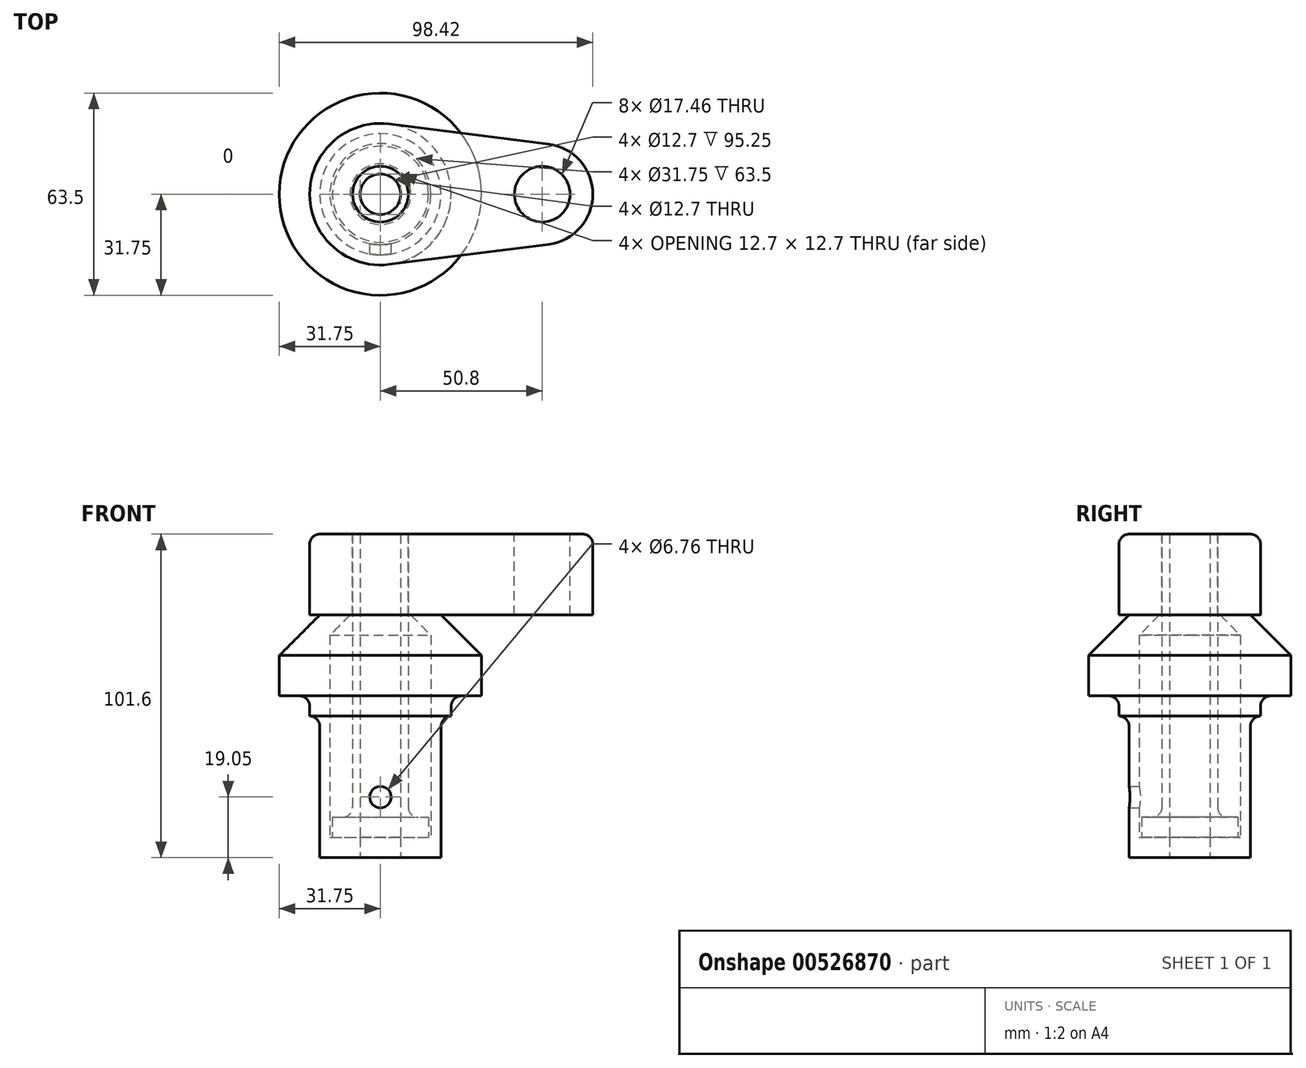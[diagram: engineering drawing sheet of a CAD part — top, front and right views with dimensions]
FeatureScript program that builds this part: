
annotation { "Feature Type Name" : "Feature", "Feature Type Description" : "" }
export const myFeature = defineFeature(function(context is Context, id is Id, definition is map)
    precondition{}
    {
        {
            var Q0;
            Q0=qCreatedBy(makeId("Front.planeOp"),FACE);
            var sketch = newSketch(context, id + "F0", { "sketchPlane" : qUnion([Q0])});
            skLineSegment(sketch, "E0", {"start": v(0, 0) * mm, "end": v(0, 76.2) * mm});
            skLineSegment(sketch, "E1", {"start": v(0, 76.2) * mm, "end": v(19.05, 76.2) * mm});
            skLineSegment(sketch, "E2", {"start": v(19.05, 76.2) * mm, "end": v(31.75, 63.5) * mm});
            skLineSegment(sketch, "E3", {"start": v(31.75, 63.5) * mm, "end": v(31.75, 50.8) * mm});
            skLineSegment(sketch, "E4", {"start": v(31.75, 50.8) * mm, "end": v(22.23, 50.8) * mm});
            skLineSegment(sketch, "E5", {"start": v(22.23, 50.8) * mm, "end": v(22.23, 44.45) * mm});
            skLineSegment(sketch, "E6", {"start": v(22.23, 44.45) * mm, "end": v(19.05, 44.45) * mm});
            skLineSegment(sketch, "E7", {"start": v(19.05, 44.45) * mm, "end": v(19.05, 0) * mm});
            skLineSegment(sketch, "E8", {"start": v(19.05, 0) * mm, "end": v(0, 0) * mm});
            skLineSegment(sketch, "E9", {"start": v(9.53, 76.2) * mm, "end": v(15.88, 69.85) * mm});
            skLineSegment(sketch, "E10", {"start": v(15.88, 69.85) * mm, "end": v(15.88, 6.35) * mm});
            skLineSegment(sketch, "E11", {"start": v(15.88, 6.35) * mm, "end": v(0, 6.35) * mm});
            skLineSegment(sketch, "E12", {"start": v(0, 76.2) * mm, "end": v(0, 92.63) * mm, "construction": true});
            skLineSegment(sketch, "E13", {"start": v(0, 76.2) * mm, "end": v(0, 101.6) * mm});
            skLineSegment(sketch, "E14", {"start": v(0, 101.6) * mm, "end": v(8.73, 101.6) * mm});
            skLineSegment(sketch, "E15", {"start": v(8.73, 101.6) * mm, "end": v(8.73, 12.7) * mm});
            skLineSegment(sketch, "E16", {"start": v(8.73, 12.7) * mm, "end": v(15.08, 12.7) * mm});
            skLineSegment(sketch, "E17", {"start": v(15.08, 12.7) * mm, "end": v(15.08, 6.35) * mm});
            skSolve(sketch);
        }
        {
            var Q0;
            {var subQ4=sQuery(id+"F0.wireOp",EDGE,"E2");Q0=makeQuery(id+"F0.imprint","IMPRINT",FACE,{"disambiguationData":[TD([[makeQuery(id+"F0.imprint","IMPRINT",EDGE,{"derivedFrom":subQ4}),-1.0]])]});}
            var Q1;
            Q1=sQuery(id+"F0.wireOp",EDGE,"E0");
            revolve(context, id + "F1", {"entities" : qUnion([Q0]), "axis" : qUnion([Q1]), "revolveType" : RevolveType.FULL});
        }
        {
            var Q0;
            {var subQ0=sQuery(id+"F0.wireOp",EDGE,"E13");Q0=makeQuery(id+"F0.imprint","IMPRINT",FACE,{"disambiguationData":[TD([[makeQuery(id+"F0.imprint","IMPRINT",EDGE,{"derivedFrom":subQ0}),-1.0]])]});}
            var Q1;
            {var subQ0=sQuery(id+"F0.wireOp",EDGE,"E16");Q1=makeQuery(id+"F0.imprint","IMPRINT",FACE,{"disambiguationData":[TD([[makeQuery(id+"F0.imprint","IMPRINT",EDGE,{"derivedFrom":subQ0}),-1.0]])]});}
            var Q2;
            Q2=sQuery(id+"F0.wireOp",EDGE,"E13");
            revolve(context, id + "F2", {"entities" : qUnion([Q0, Q1]), "axis" : qUnion([Q2]), "revolveType" : RevolveType.FULL});
        }
        {
            var Q0;
            Q0=makeQuery(id+"F2.opRevolve","SWEPT_FACE",FACE,{"disambiguationData":[OSD([sQuery(id+"F0.wireOp",EDGE,"E14")])]});
            var sketch = newSketch(context, id + "F3", { "sketchPlane" : qUnion([Q0])});
            skCircle(sketch, "E18", {"center": v(0, 0) * mm, "radius": 22.23 * mm});
            skCircle(sketch, "E19", {"center": v(50.8, 0) * mm, "radius": 15.88 * mm});
            skLineSegment(sketch, "E20", {"start": v(52.78, -15.75) * mm, "end": v(2.78, -22.05) * mm});
            skLineSegment(sketch, "E21", {"start": v(2.78, 22.05) * mm, "end": v(52.78, 15.75) * mm});
            skCircle(sketch, "E22.0", {"center": v(0, 0) * mm, "radius": 8.73 * mm});
            skCircle(sketch, "E23", {"center": v(50.8, 0) * mm, "radius": 8.73 * mm});
            skSolve(sketch);
        }
        {
            var Q0;
            Q0 = qSketchRegion(id + "F3", true);
            var Q1;
            Q1=makeQuery(id+"F1.opRevolve","SWEPT_FACE",FACE,{"disambiguationData":[OSD([sQuery(id+"F0.wireOp",EDGE,"E1")])]});
            extrude(context, id + "F4", {"entities" : qUnion([Q0]), "oppositeDirection" : true, "depth" : 25.4 * mm, "endBoundEntityFace" : qUnion([Q1]), "offsetDistance" : 0.8 * mm});
        }
        {
            var Q0;
            Q0=qCreatedBy(makeId("Front.planeOp"),FACE);
            var sketch = newSketch(context, id + "F5", { "sketchPlane" : qUnion([Q0])});
            skPoint(sketch, "E24", {"position": v(0, 19.05) * mm});
            skSolve(sketch);
        }
        {
            var Q0;
            Q0=sQuery(id+"F5.wireOp",VERTEX,"E24");
            var Q1;
            Q1=makeQuery(id+"F1.opRevolve","SWEPT_BODY",BODY,{"disambiguationData":[OSD([sQuery(id+"F0.wireOp",EDGE,"E0"),sQuery(id+"F0.wireOp",EDGE,"E1"),sQuery(id+"F0.wireOp",EDGE,"E2"),sQuery(id+"F0.wireOp",EDGE,"E3"),sQuery(id+"F0.wireOp",EDGE,"E4"),sQuery(id+"F0.wireOp",EDGE,"E5"),sQuery(id+"F0.wireOp",EDGE,"E6"),sQuery(id+"F0.wireOp",EDGE,"E7"),sQuery(id+"F0.wireOp",EDGE,"E8"),sQuery(id+"F0.wireOp",EDGE,"E9"),sQuery(id+"F0.wireOp",EDGE,"E10"),sQuery(id+"F0.wireOp",EDGE,"E11")])]});
            hole(context, id + "F6", {"style" : HoleStyle.SIMPLE, "endStyle" : HoleEndStyle.THROUGH, "oppositeDirection" : true, "standardTappedOrClearance" : lookupTablePath({ "standard" : "ANSI", "fit" : "Normal (ASME)", "size" : "1/4", "type" : "Clearance" }), "standardBlindInLast" : lookupTablePath({ "fit" : "Free", "standard" : "ANSI", "size" : "1/4", "type" : "Clearance" }), "holeDiameter" : 6.76 * mm, "tappedDepth" : 14.3 * mm, "tapClearance" : 3, "locations" : qUnion([Q0]), "scope" : qUnion([Q1])});
        }
        {
            var Q0;
            Q0=makeQuery(id+"F4.opExtrude","CAP_EDGE",EDGE,{"disambiguationData":[OSD([sQuery(id+"F3.wireOp",EDGE,"E21")])],"isStart":true});
            var Q1;
            Q1=makeQuery(id+"F1.opRevolve","SWEPT_EDGE",EDGE,{"disambiguationData":[OSD([sQuery(id+"F0.wireOp",EDGE,"E4"),sQuery(id+"F0.wireOp",EDGE,"E5")])]});
            var Q2;
            Q2=makeQuery(id+"F2.opRevolve","SWEPT_EDGE",EDGE,{"disambiguationData":[OSD([sQuery(id+"F0.wireOp",EDGE,"E15"),sQuery(id+"F0.wireOp",EDGE,"E16")])]});
            var Q3;
            Q3=makeQuery(id+"F1.opRevolve","SWEPT_EDGE",EDGE,{"disambiguationData":[OSD([sQuery(id+"F0.wireOp",EDGE,"E6"),sQuery(id+"F0.wireOp",EDGE,"E7")])]});
            fillet(context, id + "F7", {"entities" : qUnion([Q0, Q1, Q2, Q3]), "radius" : 3.17 * mm, "tangentPropagation" : true, "allowEdgeOverflow" : false});
        }
        {
            var Q0;
            Q0=makeQuery(id+"F1.opRevolve","SWEPT_FACE",FACE,{"disambiguationData":[OSD([sQuery(id+"F0.wireOp",EDGE,"E8")])]});
            var sketch = newSketch(context, id + "F8", { "sketchPlane" : qUnion([Q0])});
            skCircle(sketch, "E25", {"center": v(0, 0) * mm, "radius": 6.35 * mm});
            skSolve(sketch);
        }
        {
            var Q0;
            Q0 = qSketchRegion(id + "F8", true);
            extrude(context, id + "F9", {"entities" : qUnion([Q0]), "operationType" : NewBodyOperationType.REMOVE, "endBound" : BoundingType.THROUGH_ALL, "oppositeDirection" : true, "depth" : 25.4 * mm, "offsetDistance" : 25.4 * mm});
        }
    });
